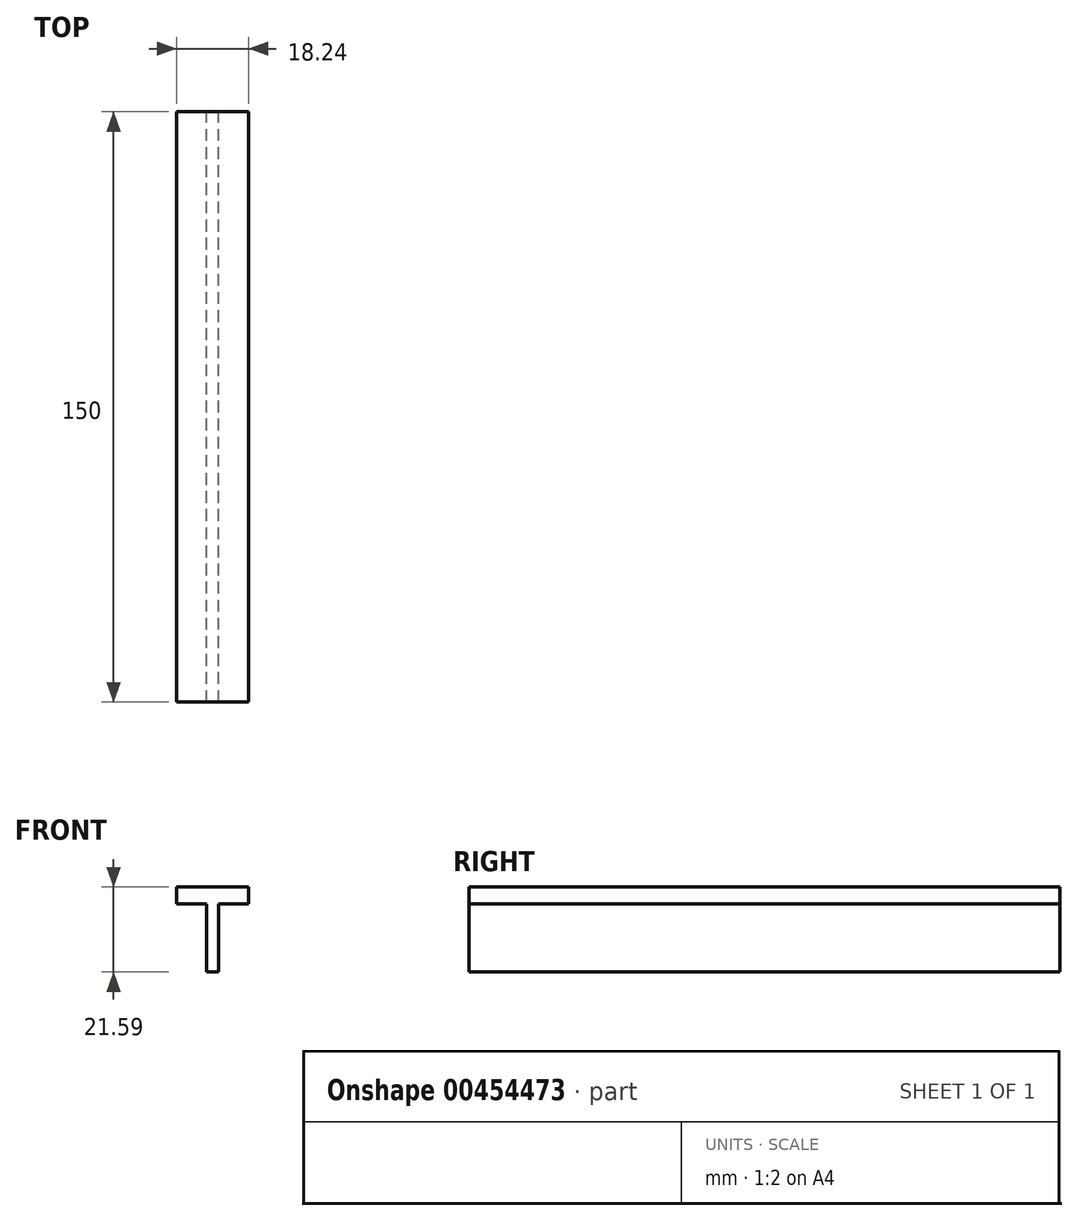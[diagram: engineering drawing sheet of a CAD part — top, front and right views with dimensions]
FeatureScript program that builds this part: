
annotation { "Feature Type Name" : "Feature", "Feature Type Description" : "" }
export const myFeature = defineFeature(function(context is Context, id is Id, definition is map)
    precondition{}
    {
        {
            var Q0;
            Q0=qCreatedBy(makeId("Front.planeOp"),FACE);
            var sketch = newSketch(context, id + "F0", { "sketchPlane" : qUnion([Q0])});
            skLineSegment(sketch, "E0.top", {"start": v(-9.12, -4.32) * mm, "end": v(-1.5, -4.32) * mm});
            skLineSegment(sketch, "E0.left", {"start": v(-9.12, 0) * mm, "end": v(-9.12, -4.32) * mm});
            skLineSegment(sketch, "E1.top", {"start": v(-1.5, -21.59) * mm, "end": v(0, -21.59) * mm});
            skLineSegment(sketch, "E1.left", {"start": v(-1.5, -4.32) * mm, "end": v(-1.5, -21.59) * mm});
            skLineSegment(sketch, "E2", {"start": v(-9.12, 0) * mm, "end": v(0, 0) * mm});
            skLineSegment(sketch, "E3", {"start": v(0, 4.88) * mm, "end": v(0, -26.17) * mm, "construction": true});
            skLineSegment(sketch, "E4", {"start": v(0, 0) * mm, "end": v(9.12, 0) * mm});
            skLineSegment(sketch, "E5", {"start": v(9.12, 0) * mm, "end": v(9.12, -4.32) * mm});
            skLineSegment(sketch, "E6", {"start": v(9.12, -4.32) * mm, "end": v(1.5, -4.32) * mm});
            skLineSegment(sketch, "E7", {"start": v(1.5, -4.32) * mm, "end": v(1.5, -21.59) * mm});
            skLineSegment(sketch, "E8", {"start": v(1.5, -21.59) * mm, "end": v(0, -21.59) * mm});
            skSolve(sketch);
        }
        {
            var Q0;
            Q0 = qSketchRegion(id + "F0", true);
            extrude(context, id + "F1", {"entities" : qUnion([Q0]), "depth" : 150 * mm});
        }
    });
